# Revit family: 306_A99X001
name_source: partatom
category: Pipe Accessories
revit_build: Autodesk Revit 2018 (Build: 20170223_1515(x64)
units: mm (PartAtom-declared; Revit-internal decimal feet)

## family parameters
Always vertical = Yes
Cut with Voids When Loaded = No
Part Type = Valve - Breaks Into
Round Connector Dimension = Use Diameter
Shared = No
Work Plane-Based = No

## types (1)
- A99X001
    A1 = 60.00°
    A2 = 120.00°
    D = 65 mm
    D2 = 40 mm
    DB1 = 52 mm  [stored 0.170604 ft]
    DB2 = 70 mm  [stored 0.229659 ft]
    DM = 90 mm  [stored 0.295276 ft]
    HDT = 4 mm  [stored 0.0131234 ft]
    HDT2 = 2 mm  [stored 0.00656168 ft]
    HDT__ve = -4 mm  [stored -0.0131234 ft]
    L1 = 37 mm  [stored 0.121391 ft]
    L2D = 141 mm
    L2D_Min = 3048 mm  [stored 10 ft]
    LB1 = 50 mm  [stored 0.164042 ft]
    LB2 = 52 mm  [stored 0.170604 ft]
    LB22 = 26 mm  [stored 0.0853018 ft]
    LB3 = 28 mm  [stored 0.0918635 ft]
    LL = 71 mm
    MC_Default_elevation = 0 mm  [stored 0 ft]
    Manufacturer = Giacomini
    QmdConnectorList = 301;D;302;D2;303;D2
    URL = http://www.giacomini.com
    W2D = 65 mm  [stored 0.213255 ft]
    X = 22 mm
    Z = 52 mm  [stored 0.170604 ft]
    magiPartTypeId = 306
    magiProductCode = A99X001
    magiProductFamilyId = A99X001
    magiProductId = A99X001

note: [stored X ft] marks values corroborated as IEEE doubles in the binary element streams (Revit-internal decimal feet)

## geometry (parser evidence)
native form markers: Sweep x2
no freeform markers — native parametric forms only
